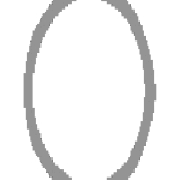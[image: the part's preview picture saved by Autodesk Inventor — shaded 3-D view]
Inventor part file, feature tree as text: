
AUTODESK INVENTOR PART (.ipt)
format: ipt  version: 2021 (Build 250183000, 183)  size: 109,568 bytes
history: native  units: in
note: dims shown in document units (in); Inventor stores cm internally (conversion verified against a paired STEP export)
features: other x4, sketch x3, plane x1
ambient origin geometry x8: Origin, YZ Plane, XZ Plane, XY Plane, X Axis, Y Axis, Z Axis, Center Point
bodies: Solid1 (feature_tree), Body (feature_tree)
feature tree (8):
  other  "Driven Length"
  other  "Frame Generator"
  other  "Start Plane"
  other  "End Plane"
  sketch  "Sketch"  dims[d2=31.6893in d4=-0.0in d5=31.6893in d6=0.12in d7=0.0in d8=90.0deg d9=31.6893in]
  sketch  "Sketch2"  dims[d0=1.0in]
  plane  "Work Plane3"
  sketch  "Sketch3"  dims[d1=0.065in]
